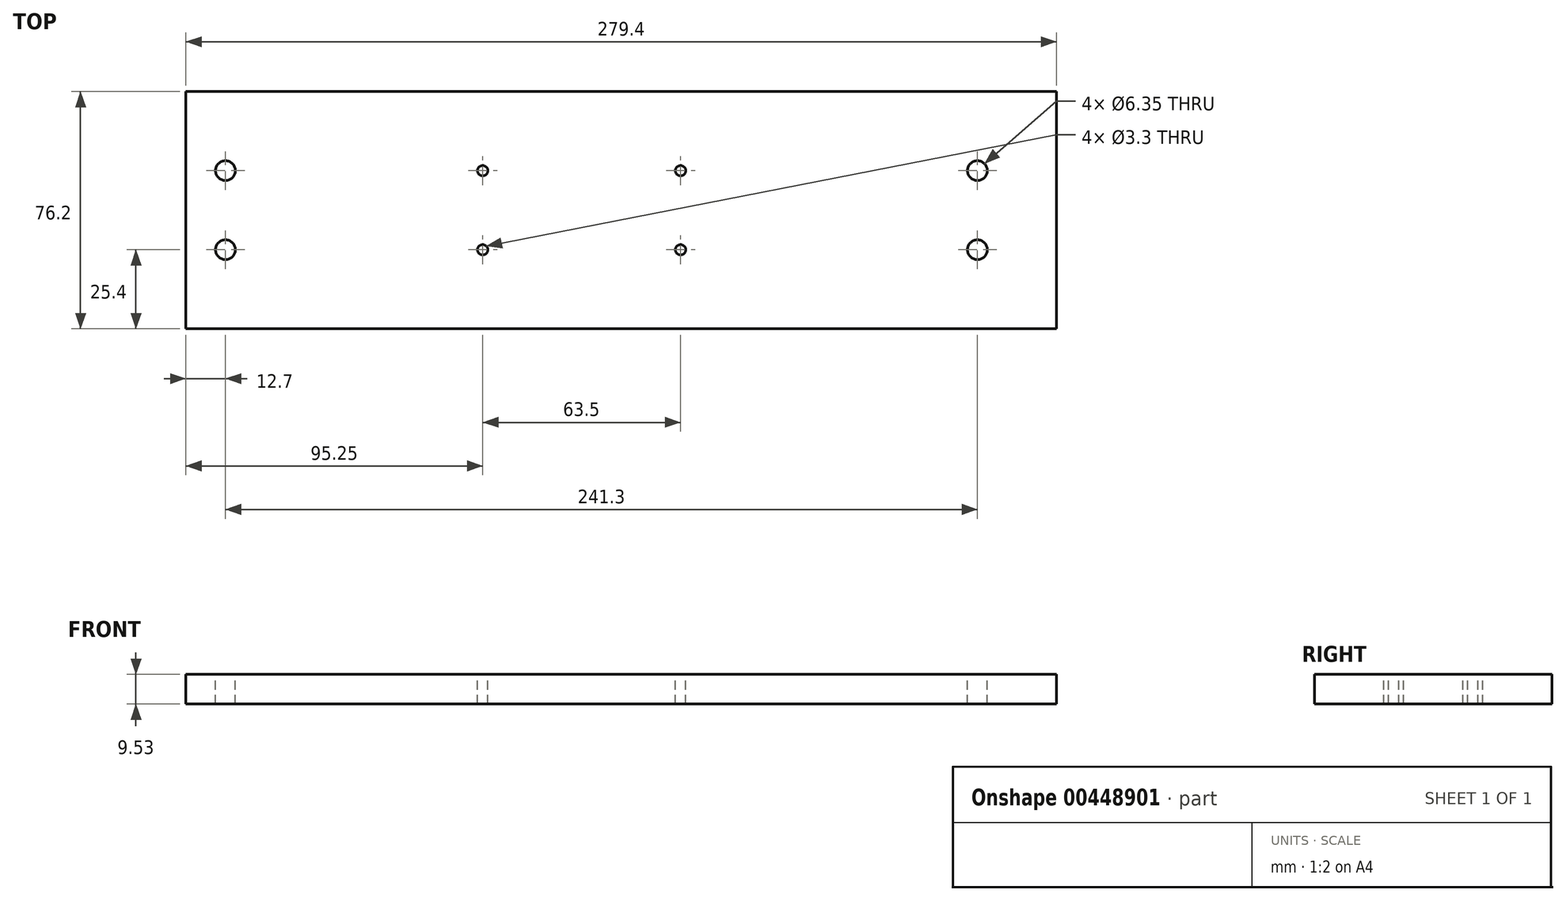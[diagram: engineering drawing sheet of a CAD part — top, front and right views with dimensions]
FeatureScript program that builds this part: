
annotation { "Feature Type Name" : "Feature", "Feature Type Description" : "" }
export const myFeature = defineFeature(function(context is Context, id is Id, definition is map)
    precondition{}
    {
        {
            var Q0;
            Q0=qCreatedBy(makeId("Top.planeOp"),FACE);
            var sketch = newSketch(context, id + "F0", { "sketchPlane" : qUnion([Q0])});
            skLineSegment(sketch, "E0.bottom", {"start": v(-139.7, 38.1) * mm, "end": v(139.7, 38.1) * mm});
            skLineSegment(sketch, "E0.top", {"start": v(-139.7, -38.1) * mm, "end": v(139.7, -38.1) * mm});
            skLineSegment(sketch, "E0.left", {"start": v(-139.7, 38.1) * mm, "end": v(-139.7, -38.1) * mm});
            skLineSegment(sketch, "E0.right", {"start": v(139.7, 38.1) * mm, "end": v(139.7, -38.1) * mm});
            skCircle(sketch, "E1", {"center": v(-127, -12.7) * mm, "radius": 3.18 * mm});
            skCircle(sketch, "E2", {"center": v(-127, 12.7) * mm, "radius": 3.18 * mm});
            skCircle(sketch, "E3", {"center": v(-44.45, -12.7) * mm, "radius": 1.65 * mm});
            skCircle(sketch, "E4", {"center": v(-44.45, 12.7) * mm, "radius": 1.65 * mm});
            skCircle(sketch, "E5", {"center": v(19.05, 12.7) * mm, "radius": 1.65 * mm});
            skCircle(sketch, "E6", {"center": v(19.05, -12.7) * mm, "radius": 1.65 * mm});
            skCircle(sketch, "E7", {"center": v(114.3, -12.7) * mm, "radius": 3.18 * mm});
            skCircle(sketch, "E8", {"center": v(114.3, 12.7) * mm, "radius": 3.18 * mm});
            skSolve(sketch);
        }
        {
            var Q0;
            Q0 = qSketchRegion(id + "F0", true);
            extrude(context, id + "F1", {"entities" : qUnion([Q0]), "oppositeDirection" : true, "depth" : 9.52 * mm});
        }
    });
